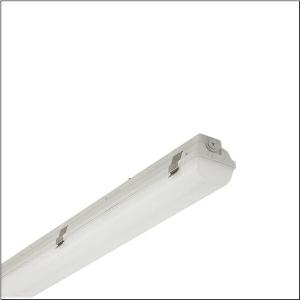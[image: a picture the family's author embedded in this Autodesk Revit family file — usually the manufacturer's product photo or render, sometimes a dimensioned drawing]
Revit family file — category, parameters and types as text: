
# Revit family: monsun_r__21_eco_51fj10dp47a_8000
name_source: partatom
category: Lighting Fixtures
units: mm (PartAtom-declared; Revit-internal decimal feet)

## family parameters
Cut with Voids When Loaded = No
Host = Face
Light Source = No
Part Type = Normal
Room Calculation Point = No
Round Connector Dimension = Use Diameter
Shared = No

## types (1)
- Monsun® 21 Eco (1 x LED, 7000 lm, 50 W, 4000K)
    Apparent Load = 50 VA
    CIE Flux Codes = 41 70 89 90 100
    Color Rendering = 80
    Color Temperature = 4000K
    Default Elevation = 1800 mm
    Description = Monsun® 21 Eco, damp-proof luminaire, primary optical cover: diffuser, of PMMA, frosted, light emission: direct distribution, primary light characteristic: symmetric, installation type: suspended mounting, surface-mounted, LED, rated luminous flux: 7.000lm, luminous efficacy: 140lm/W, light colour: 840, colour temperature: 4000K, control gear: ECG DALI, with terminal, 5-pole, max. 2.5mm², mains connection: 220..240V, AC, 50/60Hz, rated input power: 50W, housing, of glass-fibre reinforced polyester, light grey (RAL 7035), length: 1.577mm, width: 90mm, height: 95mm, clip for enclosure, of spring steel V2A, protection rating (complete): IP66, insulation class (complete): insulation class I (protective earthing), certification: CE, UKCA, protection symbol: D, impact resistance: IK02, permissible operating ambient temperature: -20..+35°C, corresponds to IFS (International Featured Standards) requirements for safety and quality in the food industry, contact your sales advisor before using the luminaires in applications with unclear chemical exposure, large temperature fluctuations or condensation-forming humidity, packaging unit: 1 piece
    Height = 103 mm
    Lamp = 1 x LED
    Lamp Light Flux = 7000 lm
    Lamp Power = 50 W
    Lamp count = 1
    Length = 1577 mm
    Luminous efficacy = 140 lm/W
    Manufacturer = Siteco
    ModVariant = No
    Model = 51FJ10DP47A
    Mounting Place = Ceiling
    Mounting Type = Surface mounted
    Number of Poles = 1
    OnlyDefault = Yes
    Power Factor = 1
    Product Name = Monsun® 21 Eco
    Product group = damp-proof luminaire
    ProductGroupID = 300
    Protection Class = Protection class I
    Protection Degree = IP 66
    RLX_Detail_Level = 1
    RLX_Emergency_Light_Flux = 0 lm
    RLX_Emergency_Type = 0
    RLX_Emergency_Type_DB = No
    RlxData = <blob elided: 33485 chars, md5=312b242c>
    Socket = socket
    Standby Power = 0 W
    System Light Flux = 7000 lm
    System Power = 50 W
    Type Comments = Product without accessories
    Type Image = l_1007218.jpg
    URL = http://relux.com
    VarID = ---
    Voltage = 0 V
    Weight = 0.00 kg
    Width = 90 mm

## geometry (parser evidence)
native form markers: Blend x4, Sweep x13
no freeform markers — native parametric forms only
